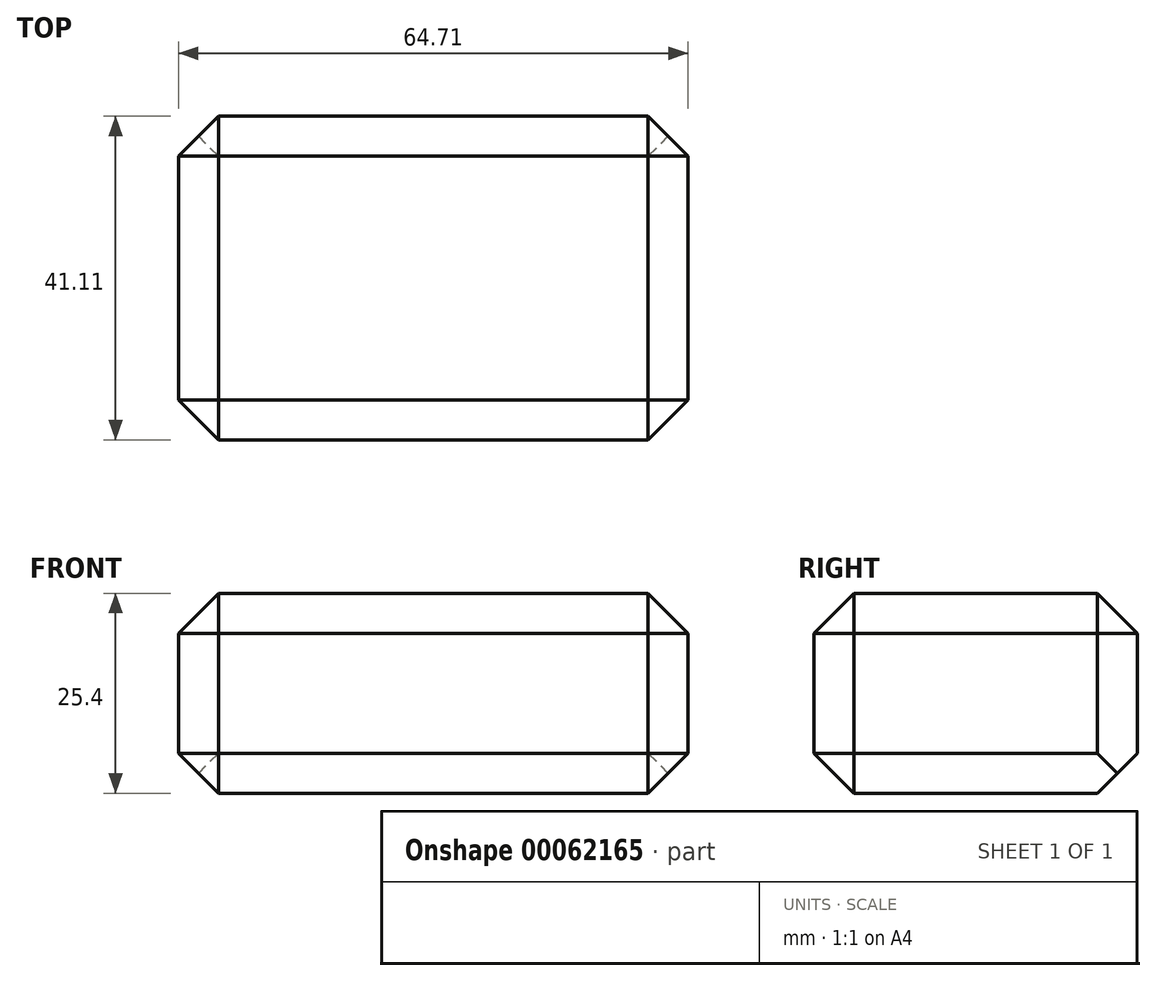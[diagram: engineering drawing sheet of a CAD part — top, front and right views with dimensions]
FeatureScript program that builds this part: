
annotation { "Feature Type Name" : "Feature", "Feature Type Description" : "" }
export const myFeature = defineFeature(function(context is Context, id is Id, definition is map)
    precondition{}
    {
        {
            var Q0;
            Q0=qCreatedBy(makeId("Top.planeOp"),FACE);
            var sketch = newSketch(context, id + "F0", { "sketchPlane" : qUnion([Q0])});
            skLineSegment(sketch, "E0.bottom", {"start": v(-27.27, 12.82) * mm, "end": v(37.44, 12.82) * mm});
            skLineSegment(sketch, "E0.top", {"start": v(-27.27, -28.29) * mm, "end": v(37.44, -28.29) * mm});
            skLineSegment(sketch, "E0.left", {"start": v(-27.27, 12.82) * mm, "end": v(-27.27, -28.29) * mm});
            skLineSegment(sketch, "E0.right", {"start": v(37.44, 12.82) * mm, "end": v(37.44, -28.29) * mm});
            skSolve(sketch);
        }
        {
            var Q0;
            Q0=makeQuery(id+"F0.imprint","IMPRINT",FACE,{"disambiguationData":[TD([[makeQuery(id+"F0.imprint","IMPRINT",EDGE,{"derivedFrom":sQuery(id+"F0.wireOp",EDGE,"E0.bottom")}),-1.0]])]});
            extrude(context, id + "F1", {"entities" : qUnion([Q0]), "depth" : 25.4 * mm});
        }
        {
            var Q0;
            Q0=makeQuery(id+"F1.opExtrude","CAP_EDGE",EDGE,{"disambiguationData":[OSD([sQuery(id+"F0.wireOp",EDGE,"E0.bottom")])],"isStart":false});
            var Q1;
            Q1=makeQuery(id+"F1.opExtrude","CAP_EDGE",EDGE,{"disambiguationData":[OSD([sQuery(id+"F0.wireOp",EDGE,"E0.right")])],"isStart":true});
            var Q2;
            Q2=makeQuery(id+"F1.opExtrude","SWEPT_EDGE",EDGE,{"disambiguationData":[OSD([sQuery(id+"F0.wireOp",EDGE,"E0.bottom"),sQuery(id+"F0.wireOp",EDGE,"E0.right")])]});
            var Q3;
            Q3=makeQuery(id+"F1.opExtrude","SWEPT_EDGE",EDGE,{"disambiguationData":[OSD([sQuery(id+"F0.wireOp",EDGE,"E0.bottom"),sQuery(id+"F0.wireOp",EDGE,"E0.left")])]});
            var Q4;
            Q4=makeQuery(id+"F1.opExtrude","CAP_EDGE",EDGE,{"disambiguationData":[OSD([sQuery(id+"F0.wireOp",EDGE,"E0.left")])],"isStart":false});
            var Q5;
            Q5=makeQuery(id+"F1.opExtrude","CAP_EDGE",EDGE,{"disambiguationData":[OSD([sQuery(id+"F0.wireOp",EDGE,"E0.left")])],"isStart":true});
            var Q6;
            Q6=makeQuery(id+"F1.opExtrude","SWEPT_EDGE",EDGE,{"disambiguationData":[OSD([sQuery(id+"F0.wireOp",EDGE,"E0.top"),sQuery(id+"F0.wireOp",EDGE,"E0.left")])]});
            var Q7;
            Q7=makeQuery(id+"F1.opExtrude","CAP_EDGE",EDGE,{"disambiguationData":[OSD([sQuery(id+"F0.wireOp",EDGE,"E0.top")])],"isStart":true});
            var Q8;
            Q8=makeQuery(id+"F1.opExtrude","CAP_EDGE",EDGE,{"disambiguationData":[OSD([sQuery(id+"F0.wireOp",EDGE,"E0.top")])],"isStart":false});
            var Q9;
            Q9=makeQuery(id+"F1.opExtrude","SWEPT_EDGE",EDGE,{"disambiguationData":[OSD([sQuery(id+"F0.wireOp",EDGE,"E0.top"),sQuery(id+"F0.wireOp",EDGE,"E0.right")])]});
            var Q10;
            Q10=makeQuery(id+"F1.opExtrude","CAP_EDGE",EDGE,{"disambiguationData":[OSD([sQuery(id+"F0.wireOp",EDGE,"E0.right")])],"isStart":false});
            chamfer(context, id + "F2", {"entities" : qUnion([Q0, Q1, Q2, Q3, Q4, Q5, Q6, Q7, Q8, Q9, Q10]), "width" : 5.08 * mm, "tangentPropagation" : true});
        }
        {
            var Q0;
            Q0=makeQuery(id+"F1.opExtrude","CAP_EDGE",EDGE,{"disambiguationData":[OSD([sQuery(id+"F0.wireOp",EDGE,"E0.bottom")])],"isStart":true});
            chamfer(context, id + "F3", {"entities" : qUnion([Q0]), "width" : 5.08 * mm, "tangentPropagation" : true});
        }
    });
